# Revit family: BuzziSpace - BuzziReDesk
name_source: partatom
category: Furniture Systems
units: mm (PartAtom-declared; Revit-internal decimal feet)

## family parameters
Always vertical = Yes
Cut with Voids When Loaded = No
Part Type = Normal
Room Calculation Point = No
Round Connector Dimension = Use Diameter
Shared = No
Work Plane-Based = No

## types (21) — shared parameters
Manufacturer = BuzziSpace
Model = BuzziReDesk
URL = https://www.buzzi.space

## per-type parameters (varying)
| type | Height | Width |
| 40cm x 80cm | 1' - 3 3/4" | 2' - 7 1/2" |
| 40cm x 100cm | 1' - 3 3/4" | 3' - 3 3/8" |
| 40cm x 120cm | 1' - 3 3/4" | 3' - 11 1/4" |
| 40cm x 140cm | 1' - 3 3/4" | 4' - 7 1/8" |
| 40cm x 160cm | 1' - 3 3/4" | 5' - 3" |
| 40cm x 180cm | 1' - 3 3/4" | 5' - 10 7/8" |
| 40cm x 200cm | 1' - 3 3/4" | 6' - 6 3/4" |
| 50cm x 80cm | 1' - 7 11/16" | 2' - 7 1/2" |
| 50cm x 100cm | 1' - 7 11/16" | 3' - 3 3/8" |
| 50cm x 120cm | 1' - 7 11/16" | 3' - 11 1/4" |
| 50cm x 140cm | 1' - 7 11/16" | 4' - 7 1/8" |
| 50cm x 160cm | 1' - 7 11/16" | 5' - 3" |
| 50cm x 180cm | 1' - 7 11/16" | 5' - 10 7/8" |
| 50cm x 200cm | 1' - 7 11/16" | 6' - 6 3/4" |
| 60cm x 80cm | 1' - 11 5/8" | 2' - 7 1/2" |
| 60cm x 100cm | 1' - 11 5/8" | 3' - 3 3/8" |
| 60cm x 120cm | 1' - 11 5/8" | 3' - 11 1/4" |
| 60cm x 140cm | 1' - 11 5/8" | 4' - 7 1/8" |
| 60cm x 160cm | 1' - 11 5/8" | 5' - 3" |
| 60cm x 180cm | 1' - 11 5/8" | 5' - 10 7/8" |
| 60cm x 200cm | 1' - 11 5/8" | 6' - 6 3/4" |

## geometry (parser evidence)
native form markers: Sweep x2
no freeform markers — native parametric forms only
